# Revit family: Hager-VEGAD-Flush_mounted-IP30-Without_Cover-With_DIN-Hosted-ES-es
name_source: partatom
category: Electrical Equipment
units: mm (PartAtom-declared; Revit-internal decimal feet)

## family parameters
Cut with Voids When Loaded = No
Host = Face
Maintain Annotation Orientation = Yes
Panel Configuration = Two Columns, Circuits Across
Part Type = Panelboard
Room Calculation Point = No
Round Connector Dimension = Use Diameter
Shared = No

## types (11) — shared parameters
BC_MODEL_ID = 1547009
BC_OBJECT_ID = 513436
BC_OBJECT_VERSION = #3
Code hager = ADD-EC000214_EU
EF000007 - Color = Blanco
EF000008 - Anchura = 600 mm
EF000024 - Resistente a UV = No
EF000116 - Número RAL = 9010
EF000118 - Con placa de montaje = No
EF000218 - Profundidad de instalación = 110 mm  [stored 0.360892 ft]
EF000846 - Anchura de montaje = 600 mm
EF001062 - Versión de CEM = No
EF001134 - Carril DIN = Yes
EF002950 - Ancho en número de espacios modulares = 24
EF005474 - Grado de protección (IP) = IP30
EF006244 - Tapa/puerta transparente = No
EF006306 - Con candado = No
EF009212 - Versión de la cubierta = Con muesca
EF015777 - Borne neutro = No
EF015941 - Puerta de transmisión de señal = No
ETIM class code = EC000214
ETIM class name = Small distribution board
HG000001 - Número de columnas = 1
HG000002-with door or cover-es = No
HG000003-Range-es = VEGAD
HG000005-Thickness-es = 2 mm  [stored 0.00656168 ft]
HG000006-Flush mounted-es = Yes
HG000009-Double swing door-es = No
HG000010-Asymmetric doors-es = No
HG000011-Empty rows from bottom-es = No
HG000012-Door swing angle-es = 90.00°
HG000013-Door on the left-es = No
HG000014-Door on the right-es = Yes
HG000015-Clearance visibility-es = Yes
HG000016-Door 3D visibility-es = Yes
HG000017-Distance between poles-es = 18 mm  [stored 0.0590551 ft]
HG000060-RAL-number = 9010
HG000099-Onfly Template ID-es-ES = 507532
HGEF0002950-Ancho en número de espacios modulares = 24
Manufacturer = Hager
Name = VEGAD-Flush_mounted-IP30-Without_Cover-With_DIN-ES
Name BIM&CO = Electricity
Name hager = ADD_Enclosures_EC000214
Uniformat = Low Tension Service & Dist.
Uniformat code = D501001
zero-valued in all types: Default Elevation, EF001131 - Profundidad interna, HG000007-Number of empty columns-es

## per-type parameters (varying)
| type | BC_VARIANT_ID | EF000003 - Método de montaje | EF000040 - Altura | EF000049 - Profundidad | EF000266 - Número de filas | EF000332 - Altura de la instalación | EF001088 - Posibilidad de extensión | EF004462 - Tipo de cierre | EF015776 - Borne de tierra | HG000004-Manufacturer reference-es | HG000008-Number of empty rows-es | HGEF000266-Número de filas |
| VEGAD-Flush_mounted_W600_H537_D150_24_Modular_Spacing-FU22DN | 1173811 | Montado empotrado (escayola) | 537 mm  [stored 1.76181 ft] | 150 mm | 2 | 537 mm  [stored 1.76181 ft] | Yes |  | No | FU22DN | 0 | 2 |
| VEGAD-Flush_mounted_W600_H687_D182_24_Modular_Spacing-FU32AN | 1173812 | Montado empotrado (escayola) | 687 mm  [stored 2.25394 ft] | 182 mm  [stored 0.597113 ft] | 3 | 687 mm  [stored 2.25394 ft] | Yes |  | No | FU32AN | 2 | 3 |
| VEGAD-Flush_mounted_W600_H687_D150_24_Modular_Spacing-FU32DN | 1173813 | Montado empotrado (escayola) | 687 mm  [stored 2.25394 ft] | 150 mm | 3 | 687 mm  [stored 2.25394 ft] | Yes |  | No | FU32DN | 0 | 3 |
| VEGAD-Flush_mounted_W600_H837_D182_24_Modular_Spacing-FU42AN | 1173814 | Montado empotrado (escayola) | 837 mm  [stored 2.74606 ft] | 182 mm  [stored 0.597113 ft] | 4 | 837 mm  [stored 2.74606 ft] | Yes |  | No | FU42AN | 2 | 4 |
| VEGAD-Flush_mounted_W600_H837_D150_24_Modular_Spacing-FU42DN | 1173815 | Montado empotrado (escayola) | 837 mm  [stored 2.74606 ft] | 150 mm | 4 | 837 mm  [stored 2.74606 ft] | Yes |  | No | FU42DN | 0 | 4 |
| VEGAD-Flush_mounted_W600_H987_D182_24_Modular_Spacing-FU52AN | 1173816 | Montado empotrado (escayola) | 987 mm  [stored 3.23819 ft] | 182 mm  [stored 0.597113 ft] | 5 | 987 mm  [stored 3.23819 ft] | Yes |  | No | FU52AN | 2 | 5 |
| VEGAD-Flush_mounted_W600_H987_D150_24_Modular_Spacing-FU52DN | 1173817 | Montaje empotrado/pared hueca | 987 mm  [stored 3.23819 ft] | 150 mm | 5 | 987 mm  [stored 3.23819 ft] | No | Otros | Yes | FU52DN | 0 | 5 |
| VEGAD-Flush_mounted_W600_H1137_D182_24_Modular_Spacing-FU62AN | 1173818 | Montaje empotrado/pared hueca | 1137 mm  [stored 3.73031 ft] | 182 mm  [stored 0.597113 ft] | 6 | 1137 mm  [stored 3.73031 ft] | No | Otros | Yes | FU62AN | 2 | 6 |
| VEGAD-Flush_mounted_W600_H1137_D150_24_Modular_Spacing-FU62DN | 1173819 | Montaje empotrado/pared hueca | 1137 mm  [stored 3.73031 ft] | 150 mm | 6 | 1137 mm  [stored 3.73031 ft] | No | Otros | Yes | FU62DN | 0 | 6 |
| VEGAD-Flush_mounted_W600_H1287_D182_24_Modular_Spacing-FU72AN | 1173820 | Montaje empotrado/pared hueca | 1287 mm  [stored 4.22244 ft] | 182 mm  [stored 0.597113 ft] | 7 | 1287 mm  [stored 4.22244 ft] | No | Otros | Yes | FU72AN | 2 | 7 |
| VEGAD-Flush_mounted_W600_H1287_D150_24_Modular_Spacing-FU72DN | 1173821 | Montaje empotrado/pared hueca | 1287 mm  [stored 4.22244 ft] | 150 mm | 7 | 1287 mm  [stored 4.22244 ft] | No | Otros | Yes | FU72DN | 0 | 7 |

note: column(s) folded — value = type name in every type: Reference

note: [stored X ft] marks values corroborated as IEEE doubles in the binary element streams (Revit-internal decimal feet)

## geometry (parser evidence)
native form markers: Sweep x16
no freeform markers — native parametric forms only
